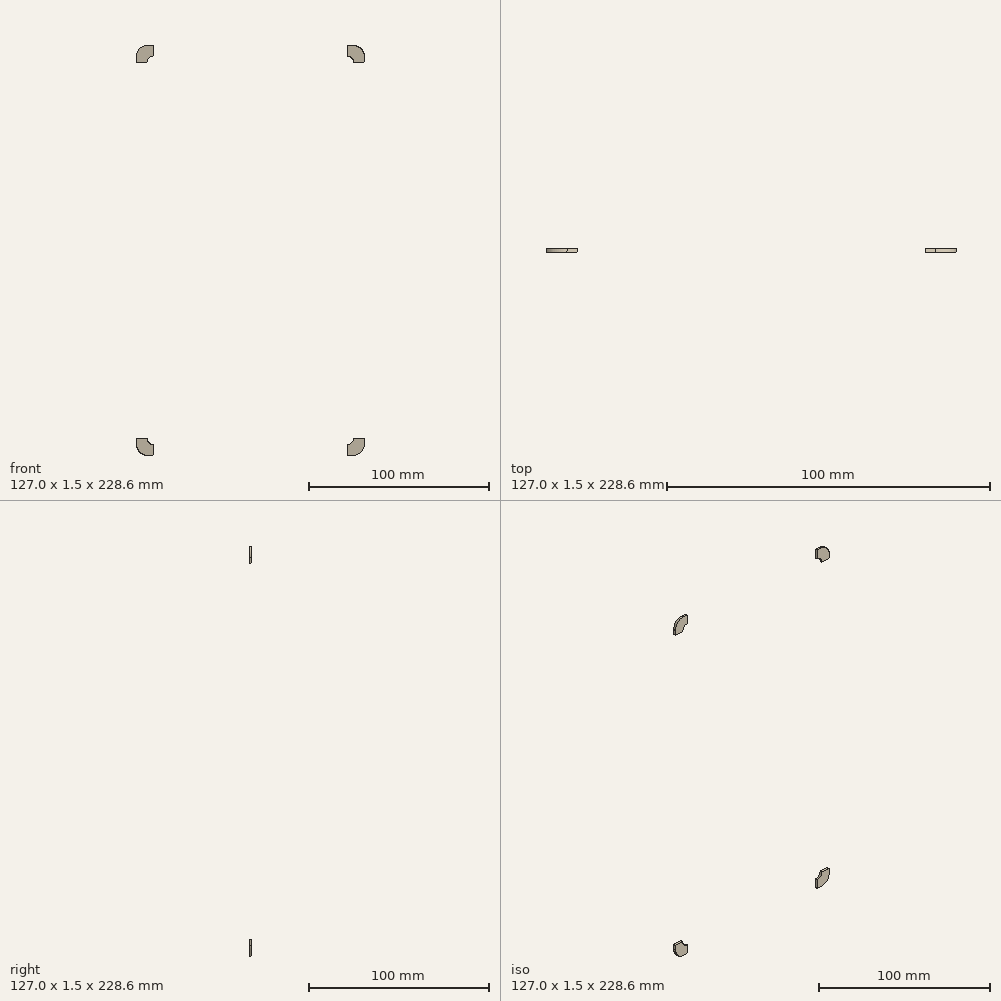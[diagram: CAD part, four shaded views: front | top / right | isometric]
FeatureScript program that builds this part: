
annotation { "Feature Type Name" : "Feature", "Feature Type Description" : "" }
export const myFeature = defineFeature(function(context is Context, id is Id, definition is map)
    precondition{}
    {
        {
            var Q0;
            Q0=qCreatedBy(makeId("Front.planeOp"),FACE);
            var sketch = newSketch(context, id + "F0", { "sketchPlane" : qUnion([Q0])});
            skLineSegment(sketch, "E0.bottom", {"start": v(-100.35, 186.64) * mm, "end": v(13.95, 186.64) * mm});
            skLineSegment(sketch, "E0.top", {"start": v(-100.35, -41.96) * mm, "end": v(13.95, -41.96) * mm});
            skLineSegment(sketch, "E0.left", {"start": v(-106.7, 180.29) * mm, "end": v(-106.7, -35.61) * mm});
            skLineSegment(sketch, "E0.right", {"start": v(20.3, 180.29) * mm, "end": v(20.3, -35.61) * mm});
            skPoint(sketch, "E1.visualSharp", {"position": v(-106.7, 186.64) * mm});
            skArc(sketch, "E1.filletArc", {"start": v(-100.35, 186.64) * mm, "mid": v(-104.84, 184.78) * mm, "end": v(-106.7, 180.29) * mm});
            skPoint(sketch, "E2.visualSharp", {"position": v(20.3, 186.64) * mm});
            skArc(sketch, "E2.filletArc", {"start": v(20.3, 180.29) * mm, "mid": v(18.44, 184.78) * mm, "end": v(13.95, 186.64) * mm});
            skPoint(sketch, "E3.visualSharp", {"position": v(-106.7, -41.96) * mm});
            skArc(sketch, "E3.filletArc", {"start": v(-106.7, -35.61) * mm, "mid": v(-104.84, -40.1) * mm, "end": v(-100.35, -41.96) * mm});
            skPoint(sketch, "E4.visualSharp", {"position": v(20.3, -41.96) * mm});
            skArc(sketch, "E4.filletArc", {"start": v(13.95, -41.96) * mm, "mid": v(18.44, -40.1) * mm, "end": v(20.3, -35.61) * mm});
            skLineSegment(sketch, "E5.bottom", {"start": v(-106.7, 186.64) * mm, "end": v(-97.17, 186.64) * mm});
            skLineSegment(sketch, "E5.top", {"start": v(-106.7, 177.11) * mm, "end": v(-97.17, 177.11) * mm});
            skLineSegment(sketch, "E5.left", {"start": v(-106.7, 186.64) * mm, "end": v(-106.7, 177.11) * mm});
            skLineSegment(sketch, "E5.right", {"start": v(-97.17, 186.64) * mm, "end": v(-97.17, 177.11) * mm});
            skCircle(sketch, "E6", {"center": v(-97.17, 177.11) * mm, "radius": 3.57 * mm});
            skLineSegment(sketch, "E7.bottom", {"start": v(20.3, 186.64) * mm, "end": v(10.78, 186.64) * mm});
            skLineSegment(sketch, "E7.top", {"start": v(20.3, 177.11) * mm, "end": v(10.78, 177.11) * mm});
            skLineSegment(sketch, "E7.left", {"start": v(20.3, 186.64) * mm, "end": v(20.3, 177.11) * mm});
            skLineSegment(sketch, "E7.right", {"start": v(10.78, 186.64) * mm, "end": v(10.78, 177.11) * mm});
            skCircle(sketch, "E8", {"center": v(10.78, 177.11) * mm, "radius": 3.57 * mm});
            skLineSegment(sketch, "E9.bottom", {"start": v(-106.7, -41.96) * mm, "end": v(-97.17, -41.96) * mm});
            skLineSegment(sketch, "E9.top", {"start": v(-106.7, -32.44) * mm, "end": v(-97.17, -32.44) * mm});
            skLineSegment(sketch, "E9.left", {"start": v(-106.7, -41.96) * mm, "end": v(-106.7, -32.44) * mm});
            skLineSegment(sketch, "E9.right", {"start": v(-97.17, -41.96) * mm, "end": v(-97.17, -32.44) * mm});
            skLineSegment(sketch, "E10.bottom", {"start": v(20.3, -41.96) * mm, "end": v(10.78, -41.96) * mm});
            skLineSegment(sketch, "E10.top", {"start": v(20.3, -32.44) * mm, "end": v(10.78, -32.44) * mm});
            skLineSegment(sketch, "E10.left", {"start": v(20.3, -41.96) * mm, "end": v(20.3, -32.44) * mm});
            skLineSegment(sketch, "E10.right", {"start": v(10.78, -41.96) * mm, "end": v(10.78, -32.44) * mm});
            skCircle(sketch, "E11", {"center": v(-97.17, -32.44) * mm, "radius": 3.57 * mm});
            skCircle(sketch, "E12", {"center": v(10.78, -32.44) * mm, "radius": 3.57 * mm});
            skSolve(sketch);
        }
        {
            var Q0;
            {var subQ3=sQuery(id+"F0.wireOp",EDGE,"E1.filletArc");Q0=makeQuery(id+"F0.imprint","IMPRINT",FACE,{"disambiguationData":[TD([[makeQuery(id+"F0.imprint","IMPRINT",EDGE,{"derivedFrom":subQ3}),1.0]])]});}
            var Q1;
            {var subQ12=sQuery(id+"F0.wireOp",EDGE,"E0.bottom");Q1=makeQuery(id+"F0.imprint","IMPRINT",FACE,{"disambiguationData":[TD([[makeQuery(id+"F0.imprint","IMPRINT",EDGE,{"derivedFrom":subQ12}),-1.0]])]});}
            var Q2;
            {var subQ3=sQuery(id+"F0.wireOp",EDGE,"E2.filletArc");Q2=makeQuery(id+"F0.imprint","IMPRINT",FACE,{"disambiguationData":[TD([[makeQuery(id+"F0.imprint","IMPRINT",EDGE,{"derivedFrom":subQ3}),1.0]])]});}
            var Q3;
            {var subQ3=sQuery(id+"F0.wireOp",EDGE,"E3.filletArc");Q3=makeQuery(id+"F0.imprint","IMPRINT",FACE,{"disambiguationData":[TD([[makeQuery(id+"F0.imprint","IMPRINT",EDGE,{"derivedFrom":subQ3}),1.0]])]});}
            var Q4;
            {var subQ3=sQuery(id+"F0.wireOp",EDGE,"E4.filletArc");Q4=makeQuery(id+"F0.imprint","IMPRINT",FACE,{"disambiguationData":[TD([[makeQuery(id+"F0.imprint","IMPRINT",EDGE,{"derivedFrom":subQ3}),1.0]])]});}
            extrude(context, id + "F1", {"entities" : qUnion([Q0, Q1, Q2, Q3, Q4]), "depth" : 1.52 * mm, "offsetDistance" : 25.4 * mm});
        }
    });
